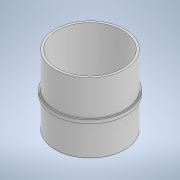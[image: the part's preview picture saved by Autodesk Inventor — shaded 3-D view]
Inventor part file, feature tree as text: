
AUTODESK INVENTOR PART (.ipt)
format: ipt  version: 2022 (Build 260153000, 153)  size: 131,072 bytes
history: native  units: mm
features: revolve x1, sketch x1
ambient origin geometry x8: Origin, YZ Plane, XZ Plane, XY Plane, X Axis, Y Axis, Z Axis, Center Point
bodies: Solid1 (feature_tree)
feature tree (2):
  revolve  "Revolution1"  [1 undecoded]
  sketch  "Sketch1"  dims[d1=100.0mm d2=50.0mm d3=5.0mm d4=3.0mm d5=99.0mm d6=103.5mm d7=90.0deg d8=1.5mm]
note: 1 required parameter value undecoded (feature->parameter linkage not recoverable at this tier; creation-order binding heuristic only, values carry confidence <= 0.55)
